# Revit family: Maxlogic détecteur de montage encastrée
name_source: partatom
category: Fire Alarm Devices
units: mm (PartAtom-declared; Revit-internal decimal feet)

## family parameters
Cut with Voids When Loaded = No
Host = Face
Maintain Annotation Orientation = Yes
OmniClass Number = 23.85.30.21
OmniClass Title = Environmental Detection/Registration
Part Type = Normal
Room Calculation Point = No
Round Connector Dimension = Use Diameter
Shared = No

## types (10) — shared parameters
Adresse ligne 1 = Şerifali Mahallesi Kutup Sokak No:27/1-2-4 Ümraniye TR-34775 İSTANBUL
Bôitier de montage en surface étanche = ML-0121
Couleur = Blanc
Deuxième Matèriel = Plastique
Durée de la garantie  de pièces rechange = 2
Durée de la travail = 2
Hauteur Nominal = 106 mm
Largeur Nominal = 51 mm
Longeur Nominal = 106 mm
Manuel d'installation = https://mavilielektronik.com
Manufacturer = Mavili Elektronik Ticaret A.Ş.
Matèriel Principe = Plastique Blanche PC/ABS
Model = Maxlogic
Numèro de Fax = (+)90 216 466 45 10
Socle Montage de Plafond = ML-0150
Socles Compatible = ML-0140
Socles Compatible  2 = ML-0141
Tempèrature de Fonctionnement = (-10°C) - (+50°C)
URL = https://www.mavili.com.tr
Unité de durée de garantie = Ans
Voltage de fonctionnement (défaut) = 26 V/DC
zero-valued in all types: Cost, Default Elevation

## per-type parameters (varying)
| type | Cercle de Chaleur | Cercle de Multi Critière | Charger adresse d'appareil | Code de Performance | Code de Produit | Description | Détection de Radius | Numéro de pose des travaux public | Poids | Sortie d'indicateur | Surface de Montage | Voltage Fonction d'opération |
| Maxlogic Conventionnelle Détecteur de fumée optique  ,base de montage encastrèe | No | No |  | EN 54-7 | ML-2110 | Maxlogic Conventionnelle Détecteur de fumée optique  ,base de montage encastrèe | 6,2 m | 832-106 | 140 gr | MG-4000 | Montage à Plafond | 10-30V/DC |
| Maxlogic Adressable Détecteur de fumée optique ,base de montage encastrèe | No | No | Appareil d'adressage à Main | EN 54-7 | ML-1110 | Adressable Détecteur de fumée optique ,base de montage encastrèe | 6,2 m | 833-500 | 100 gr | MG-4000.A | Montage à Plafond | 18-33V/DC |
| Maxlogic Adressable Détecteur de fumée optique  ,base de montage encastrèe,Isolateur de Court-Circuit | No | No | Appareil d'adressage à Main | EN 54-7 / EN 54-17 | ML-1110.SCI | Adressable Détecteur de fumée optique  ,base de montage encastrèe,Isolateur de Court-Circuit | 6,2 m | 833-501 | 100 gr | MG-4000.A | Montage à Plafond | 18-33V/DC |
| Maxlogic Conventionnelle  Détecteur de chaleur fixe ,base de montage encastrèe | Yes | No |  | EN 54-5 | ML-2120 | Maxlogic Conventionnelle Détecteur de chaleur fixe ,base de montage encastrèe | 4,5 m | 832-102 | 135 gr | MG-4000 | Montage à Plafond | 10-30V/DC |
| Maxlogic Conventionnelle Détecteur de chaleurbase de montage encastrèe | Yes | No |  | EN 54-5 | ML-2130 | Détecteur de chaleur conventionelle,base de montage encastrèe | 4,5 m | 832-103 | 135 gr | MG-4000 | Montage à Mur | 10-30V/DC |
| Maxlogic Adressable Détecteur de chaleur combiné ,base de montage encastrèe | Yes | No | Appareil d'adressage à Main | EN 54-5 | ML-1130 | Détecteur de  chaleur combiné adressable,base de montage encastrèe | 4,5 m | 833-520 | 95 gr | MG-4000.A | Montage à Plafond | 18-33V/DC |
| Maxlogic Adressable Détecteur de chaleur combiné ,base de montage encastrèe,Isolateur de Court-Circuit | Yes | No | Appareil d'adressage à Main | EN 54-5 / EN 54-17 | ML-1130.SCI | Maxlogic Détecteur de  chaleur combiné adressable,base de montage encastrèe,Isolateur de Court-Circuit | 4,5 m | 833-521 | 95 gr | MG-4000.A | Montage à Plafond | 18-33V/DC |
| Maxlogic Conventionnelle détecteur de multi-capteur,base de montage encastrèe | Yes | Yes |  | EN 54-5 / EN 54-7 | ML-2140 | Maxlogic Conventionnelle détecteur de multi-capteur ,base de montage encastrèe | 4,5 m | 832-109 | 141 gr | MG-4000 | Montage à Plafond | 10-30V/DC |
| Maxlogic Adressable détecteur de multi-capteur  ,base de montage encastrèe , base de montage encastrèe | Yes | Yes | Appareil d'adressage à Main | EN 54-5 / EN 54-7 / EN 54-17 | ML-1140 | Maxlogic détecteur de multi-capteur Adressable ,base de montage encastrèe , base de montage encastrèe | 4,5 m | 833-530 | 100 gr | MG-4000.A | Montage à Plafond | 18-33V/DC |
| Maxlogic Adressable détecteur de multi-capteur ,base de montage encastrèe , base de montage encastrèe,Isolateur de Court-Circuit | Yes | Yes | Appareil d'adressage à Main | EN 54-5 / EN 54-7 / EN 54-17 | ML-1140.SCI | Détecteur de multi-capteur Adressable ,base de montage encastrèe , base de montage encastrèe,Isolateur de Court-Circuit | 4,5 m | 833-531 | 100 gr | MG-4000.A | Montage à Plafond | 18-33V/DC |

## geometry (parser evidence)
native form markers: Sweep x1
no freeform markers — native parametric forms only
